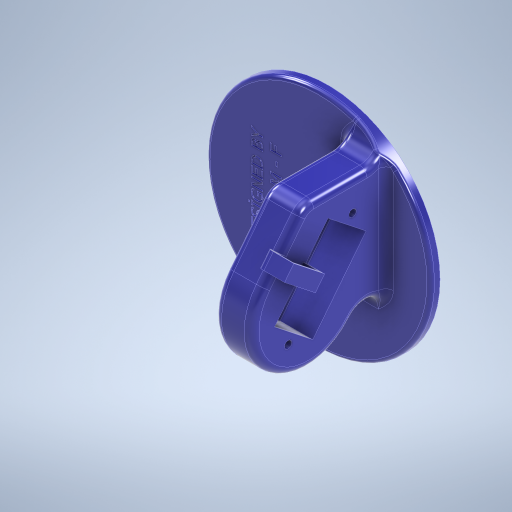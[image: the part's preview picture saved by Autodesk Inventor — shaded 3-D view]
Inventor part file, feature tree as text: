
AUTODESK INVENTOR PART (.ipt)
format: ipt  version: 2023.2 (Build 272271000, 271)  size: 834,048 bytes
history: native  units: mm
features: sketch x9, extrude x5, fillet x5, hole x3, emboss x1, plane x1
ambient origin geometry x8: Origin, YZ Plane, XZ Plane, XY Plane, X Axis, Y Axis, Z Axis, Center Point
bodies: Solid1 (feature_tree)
feature tree (24):
  extrude  "Extrusion1"  Depth=2.5mm TaperAngle=0.0deg
  hole  "Hole1"  [1 undecoded]
  hole  "Hole2"  [1 undecoded]
  emboss  "Emboss1"
  plane  "Work Plane1"
  extrude  "Extrusion2"  Depth=6.1mm
  extrude  "Extrusion5"  Depth=10.0mm
  hole  "Hole4"  [1 undecoded]
  fillet  "Fillet1"  Radius=10.0mm
  fillet  "Fillet2"  Radius=2.5mm
  fillet  "Fillet3"  Radius=8.7mm
  fillet  "Fillet4"  Radius=27.8mm
  extrude  "Extrusion6"  Depth=5.0mm
  fillet  "Fillet5"  Radius=2.0mm
  extrude  "Extrusion7"  Depth=2.0mm
  sketch  "Sketch1"  dims[d0=60.0mm d1=2.5mm d2=0.0mm]
  sketch  "Sketch2"  dims[d3=17.0mm]
  sketch  "Sketch3"  dims[d4=2.1mm d5=6.0mm d6=4.0mm d7=2.0mm d8=90.0deg d9=8.0mm d10=0.0mm]
  sketch  "Sketch4"  dims[d11=8.0mm d12=6.0mm d13=4.0mm d14=2.0mm d15=90.0deg d16=8.0mm d17=0.0mm d18=1.0mm d19=0.0mm]
  sketch  "Sketch5"  dims[d20=8.0mm d21=12.6mm]
  sketch  "Sketch10"  dims[d22=22.6mm d23=6.1mm]
  sketch  "Sketch11"  dims[d24=10.0mm d25=32.4mm]
  sketch  "Sketch12"  dims[d26=2.5mm d27=2.5mm d28=10.0mm d29=0.0mm d64=2.5mm]
  sketch  "Sketch13"  dims[d66=13.0mm d67=23.0mm d68=6.3mm d69=10.0mm d70=32.4mm d71=2.5mm d72=2.5mm d73=2.5mm d74=8.7mm d75=0.0mm d76=27.8mm d77=2.0mm d78=6.0mm d79=4.0mm d80=2.0mm d81=90.0deg d82=7.0mm d83=0.0mm d84=5.0mm d85=2.0mm d86=2.0mm d87=1.0mm d88=9.5mm d89=1.0mm d90=5.0mm d91=0.0mm d92=2.0mm d93=1.0mm d94=1.0mm d95=2.5mm d96=0.0mm d97=2.0mm d98=1.0mm d99=1.0mm d100=1.0mm d101=5.0mm d102=0.0mm]
note: 3 required parameter values undecoded (feature->parameter linkage not recoverable at this tier; creation-order binding heuristic only, values carry confidence <= 0.55)
